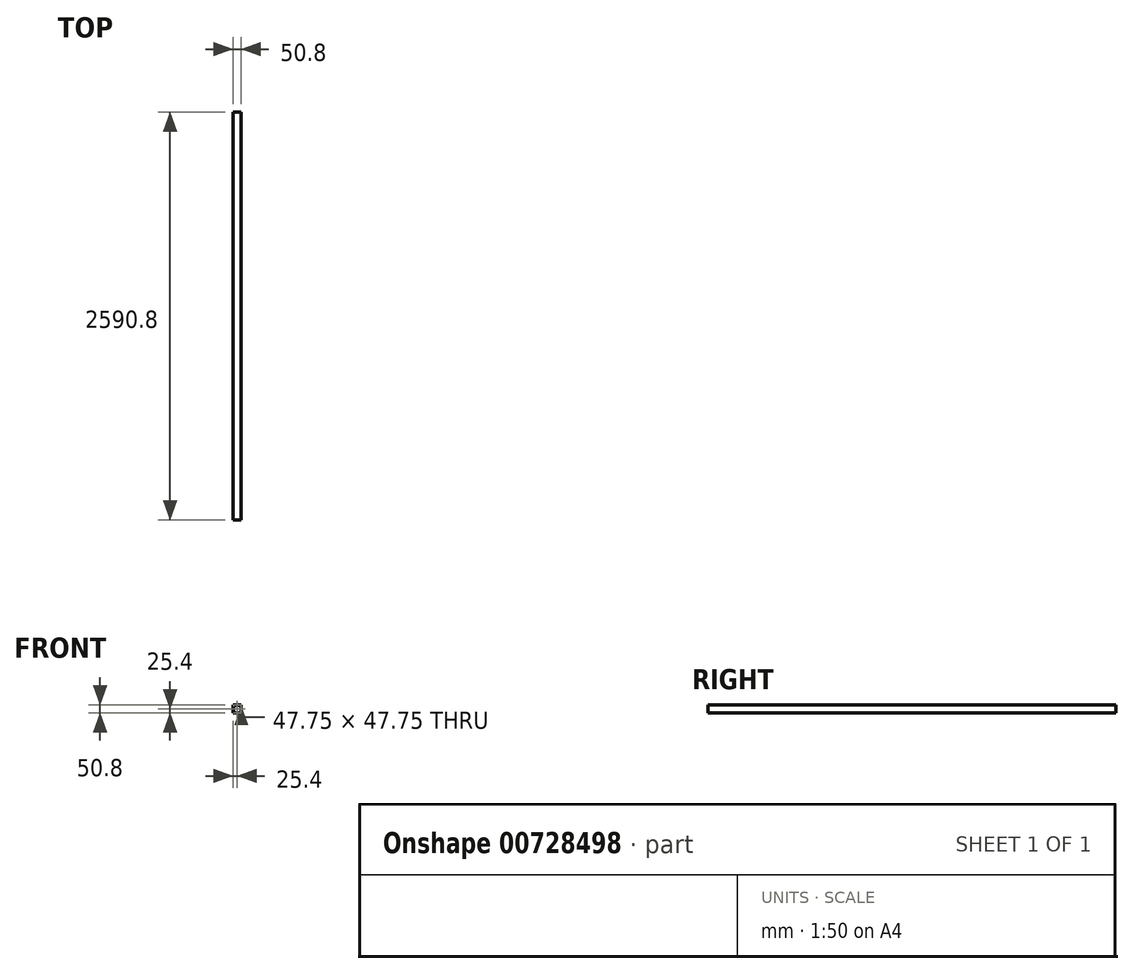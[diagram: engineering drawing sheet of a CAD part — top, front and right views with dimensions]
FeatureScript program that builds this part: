
annotation { "Feature Type Name" : "Feature", "Feature Type Description" : "" }
export const myFeature = defineFeature(function(context is Context, id is Id, definition is map)
    precondition{}
    {
        {
            var Q0;
            Q0=qCreatedBy(makeId("Front.planeOp"),FACE);
            var sketch = newSketch(context, id + "F0", { "sketchPlane" : qUnion([Q0])});
            skLineSegment(sketch, "E0.bottom", {"start": v(-25.4, 25.4) * mm, "end": v(25.4, 25.4) * mm});
            skLineSegment(sketch, "E0.top", {"start": v(-25.4, -25.4) * mm, "end": v(25.4, -25.4) * mm});
            skLineSegment(sketch, "E0.left", {"start": v(-25.4, 25.4) * mm, "end": v(-25.4, -25.4) * mm});
            skLineSegment(sketch, "E0.right", {"start": v(25.4, 25.4) * mm, "end": v(25.4, -25.4) * mm});
            skPoint(sketch, "E0.middle", {"position": v(0, 0) * mm});
            skLineSegment(sketch, "E1.bottom", {"start": v(-23.88, 23.88) * mm, "end": v(23.88, 23.88) * mm});
            skLineSegment(sketch, "E1.top", {"start": v(-23.88, -23.88) * mm, "end": v(23.88, -23.88) * mm});
            skLineSegment(sketch, "E1.left", {"start": v(-23.88, 23.88) * mm, "end": v(-23.88, -23.88) * mm});
            skLineSegment(sketch, "E1.right", {"start": v(23.88, 23.88) * mm, "end": v(23.88, -23.88) * mm});
            skSolve(sketch);
        }
        {
            var Q0;
            Q0=makeQuery(id+"F0.imprint","IMPRINT",FACE,{"disambiguationData":[TD([[makeQuery(id+"F0.imprint","IMPRINT",EDGE,{"derivedFrom":sQuery(id+"F0.wireOp",EDGE,"E0.bottom")}),-1.0]])]});
            extrude(context, id + "F1", {"entities" : qUnion([Q0]), "endBound" : BoundingType.SYMMETRIC, "depth" : 2590.8 * mm, "offsetDistance" : 25.4 * mm});
        }
    });
